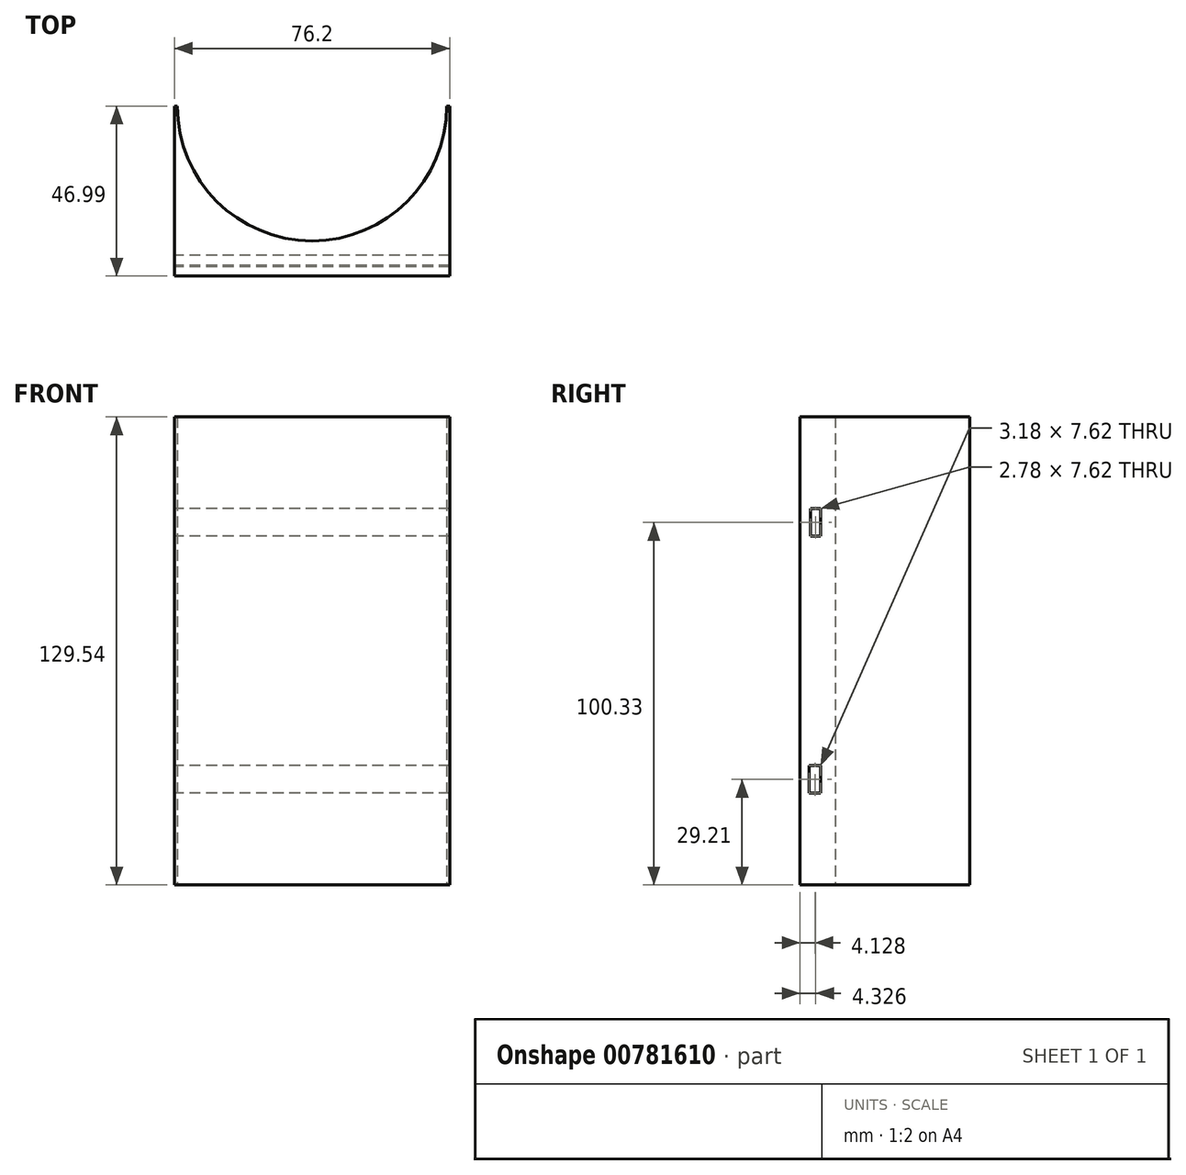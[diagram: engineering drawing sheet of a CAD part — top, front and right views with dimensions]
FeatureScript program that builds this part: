
annotation { "Feature Type Name" : "Feature", "Feature Type Description" : "" }
export const myFeature = defineFeature(function(context is Context, id is Id, definition is map)
    precondition{}
    {
        {
            var Q0;
            Q0=qCreatedBy(makeId("Front.planeOp"),FACE);
            var sketch = newSketch(context, id + "F0", { "sketchPlane" : qUnion([Q0])});
            skLineSegment(sketch, "E0.bottom", {"start": v(-38.1, 0) * mm, "end": v(38.1, 0) * mm});
            skLineSegment(sketch, "E0.top", {"start": v(-38.1, 129.54) * mm, "end": v(38.1, 129.54) * mm});
            skLineSegment(sketch, "E0.left", {"start": v(-38.1, 0) * mm, "end": v(-38.1, 129.54) * mm});
            skLineSegment(sketch, "E0.right", {"start": v(38.1, 0) * mm, "end": v(38.1, 129.54) * mm});
            skSolve(sketch);
        }
        {
            var Q0;
            Q0 = qSketchRegion(id + "F0", true);
            extrude(context, id + "F1", {"entities" : qUnion([Q0]), "depth" : 47 * mm, "offsetDistance" : 25.4 * mm});
        }
        {
            var Q0;
            Q0=qCreatedBy(makeId("Top.planeOp"),FACE);
            var sketch = newSketch(context, id + "F2", { "sketchPlane" : qUnion([Q0])});
            skCircle(sketch, "E1", {"center": v(0, 0) * mm, "radius": 37.27 * mm});
            skSolve(sketch);
        }
        {
            var Q0;
            Q0=makeQuery(id+"F2.imprint","IMPRINT",FACE,{"disambiguationData":[TD([[makeQuery(id+"F2.imprint","IMPRINT",EDGE,{"derivedFrom":sQuery(id+"F2.wireOp",EDGE,"E1")}),1.0]])]});
            extrude(context, id + "F3", {"entities" : qUnion([Q0]), "operationType" : NewBodyOperationType.REMOVE, "endBound" : BoundingType.UP_TO_NEXT, "depth" : 129.54 * mm, "offsetDistance" : 25.4 * mm});
        }
        {
            var Q0;
            Q0=makeQuery(id+"F1.opExtrude","SWEPT_FACE",FACE,{"disambiguationData":[OSD([sQuery(id+"F0.wireOp",EDGE,"E0.left")])]});
            var sketch = newSketch(context, id + "F4", { "sketchPlane" : qUnion([Q0])});
            skLineSegment(sketch, "E2.bottom", {"start": v(41.28, 25.4) * mm, "end": v(44.45, 25.4) * mm});
            skLineSegment(sketch, "E2.top", {"start": v(41.28, 33.02) * mm, "end": v(44.45, 33.02) * mm});
            skLineSegment(sketch, "E2.left", {"start": v(41.28, 25.4) * mm, "end": v(41.28, 33.02) * mm});
            skLineSegment(sketch, "E2.right", {"start": v(44.45, 25.4) * mm, "end": v(44.45, 33.02) * mm});
            skLineSegment(sketch, "E3.bottom", {"start": v(41.27, 104.14) * mm, "end": v(44.05, 104.14) * mm});
            skLineSegment(sketch, "E3.top", {"start": v(41.28, 96.52) * mm, "end": v(44.05, 96.52) * mm});
            skLineSegment(sketch, "E3.left", {"start": v(41.27, 96.52) * mm, "end": v(41.27, 104.14) * mm});
            skLineSegment(sketch, "E3.right", {"start": v(44.05, 96.52) * mm, "end": v(44.05, 104.14) * mm});
            skSolve(sketch);
        }
        {
            var Q0;
            Q0 = qSketchRegion(id + "F4", true);
            extrude(context, id + "F5", {"entities" : qUnion([Q0]), "operationType" : NewBodyOperationType.REMOVE, "endBound" : BoundingType.UP_TO_NEXT, "oppositeDirection" : true, "depth" : 25.4 * mm, "offsetDistance" : 25.4 * mm});
        }
    });
